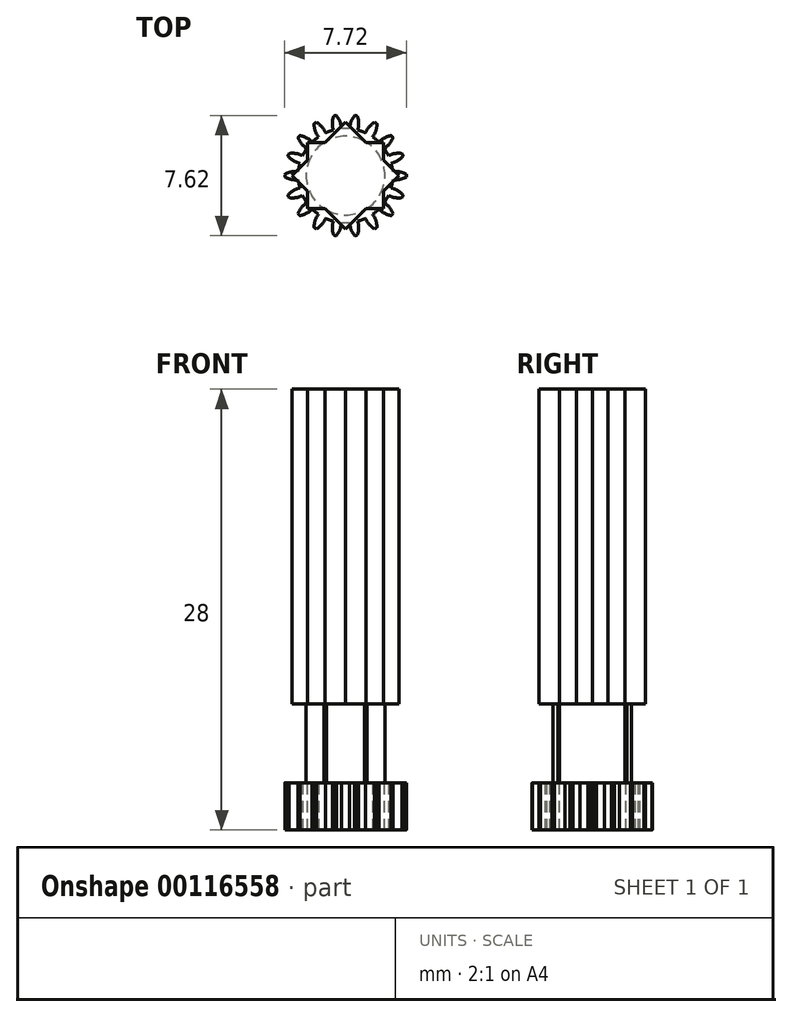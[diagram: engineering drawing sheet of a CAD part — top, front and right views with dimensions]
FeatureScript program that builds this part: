
annotation { "Feature Type Name" : "Feature", "Feature Type Description" : "" }
export const myFeature = defineFeature(function(context is Context, id is Id, definition is map)
    precondition{}
    {
        {
            var Q0;
            Q0=qCreatedBy(makeId("Top.planeOp"),FACE);
            var sketch = newSketch(context, id + "F0", { "sketchPlane" : qUnion([Q0])});
            skArc(sketch, "E0", {"start": v(2.95, 0.52) * mm, "mid": v(2.97, 0.4) * mm, "end": v(2.99, 0.26) * mm, "construction": true});
            skArc(sketch, "E1", {"start": v(2.95, 0.52) * mm, "mid": v(2.97, 0.4) * mm, "end": v(2.99, 0.26) * mm});
            skArc(sketch, "E2.MirrorCS", {"start": v(2.95, -0.52) * mm, "mid": v(2.97, -0.4) * mm, "end": v(2.99, -0.26) * mm});
            skPoint(sketch, "E3", {"position": v(3.86, 0) * mm});
            skArc(sketch, "E4", {"start": v(3.86, 0.09) * mm, "mid": v(3.44, 0.24) * mm, "end": v(2.99, 0.26) * mm});
            skArc(sketch, "E5", {"start": v(3.86, 0.09) * mm, "mid": v(3.86, 0.04) * mm, "end": v(3.86, 0) * mm});
            skLineSegment(sketch, "E6", {"start": v(0, 0) * mm, "end": v(4.16, 0) * mm, "construction": true});
            skArc(sketch, "E7.MirrorCS", {"start": v(3.86, -0.09) * mm, "mid": v(3.44, -0.24) * mm, "end": v(2.99, -0.26) * mm});
            skArc(sketch, "E8.MirrorCS", {"start": v(3.86, -0.09) * mm, "mid": v(3.86, -0.04) * mm, "end": v(3.86, 0) * mm});
            skLineSegment(sketch, "E9", {"start": v(0, 0) * mm, "end": v(2.95, 0.52) * mm});
            skLineSegment(sketch, "E10", {"start": v(0, 0) * mm, "end": v(2.95, -0.52) * mm});
            skSolve(sketch);
        }
        {
            var Q0;
            Q0=qSketchRegion(id+"F0",true);
            extrude(context, id + "F1", {"entities" : qUnion([Q0]), "depth" : 3 * mm});
        }
        {
            var Q0;
            Q0=makeQuery(id+"F1.opExtrude","SWEPT_BODY",BODY,{"disambiguationData":[OSD([sQuery(id+"F0.wireOp",EDGE,"E1"),sQuery(id+"F0.wireOp",EDGE,"E2.MirrorCS"),sQuery(id+"F0.wireOp",EDGE,"E4"),sQuery(id+"F0.wireOp",EDGE,"E5"),sQuery(id+"F0.wireOp",EDGE,"E7.MirrorCS"),sQuery(id+"F0.wireOp",EDGE,"E8.MirrorCS"),sQuery(id+"F0.wireOp",EDGE,"E9"),sQuery(id+"F0.wireOp",EDGE,"E10")])]});
            var Q1;
            Q1=makeQuery(id+"F1.opExtrude","SWEPT_EDGE",EDGE,{"disambiguationData":[OSD([sQuery(id+"F0.wireOp",EDGE,"E9"),sQuery(id+"F0.wireOp",EDGE,"E10")])]});
            circularPattern(context, id + "F2", {"operationType" : NewBodyOperationType.ADD, "entities" : qUnion([Q0]), "axis" : qUnion([Q1]), "angle" : 20 * degree, "instanceCount" : 18});
        }
        {
            var Q0;
            Q0=qSketchRegion(id+"F0",true);
            extrude(context, id + "F3", {"entities" : qUnion([Q0]), "depth" : 3 * mm});
        }
        {
            var Q0;
            Q0=makeQuery(id+"F1.opExtrude","CAP_FACE",FACE,{"disambiguationData":[OSD([sQuery(id+"F0.wireOp",EDGE,"Pb6nrEPp-SJh7-syUI-6Dz9-aLrEaNv6bWqD"),sQuery(id+"F0.wireOp",EDGE,"E1"),sQuery(id+"F0.wireOp",EDGE,"xMCTbKjx-bBFs-oRzr-sJjZ-jvfvOUALp0gi"),sQuery(id+"F0.wireOp",EDGE,"LEszv8Jj-5ZlA-iPn8-BHO1-omDbxf6y6Z2k"),sQuery(id+"F0.wireOp",EDGE,"88d082c0-6565-44ed-966f-5d657ca2ec560.MirrorCS"),sQuery(id+"F0.wireOp",EDGE,"E2.MirrorCS"),sQuery(id+"F0.wireOp",EDGE,"91265b68-e2b7-404f-b8fe-75b5f12c093b0.MirrorCS"),sQuery(id+"F0.wireOp",EDGE,"1d9e2677-8dce-4da0-891b-71f10a0ff0ad0.MirrorCS"),sQuery(id+"F0.wireOp",EDGE,"29e68c91-4fe4-4bf7-b556-72e67ca85e0b.1.0"),sQuery(id+"F0.wireOp",EDGE,"29e68c91-4fe4-4bf7-b556-72e67ca85e0b.1.1"),sQuery(id+"F0.wireOp",EDGE,"29e68c91-4fe4-4bf7-b556-72e67ca85e0b.1.2"),sQuery(id+"F0.wireOp",EDGE,"29e68c91-4fe4-4bf7-b556-72e67ca85e0b.1.3"),sQuery(id+"F0.wireOp",EDGE,"29e68c91-4fe4-4bf7-b556-72e67ca85e0b.1.4"),sQuery(id+"F0.wireOp",EDGE,"29e68c91-4fe4-4bf7-b556-72e67ca85e0b.1.5"),sQuery(id+"F0.wireOp",EDGE,"29e68c91-4fe4-4bf7-b556-72e67ca85e0b.1.7"),sQuery(id+"F0.wireOp",EDGE,"29e68c91-4fe4-4bf7-b556-72e67ca85e0b.1.8"),sQuery(id+"F0.wireOp",EDGE,"29e68c91-4fe4-4bf7-b556-72e67ca85e0b.2.0"),sQuery(id+"F0.wireOp",EDGE,"29e68c91-4fe4-4bf7-b556-72e67ca85e0b.2.1"),sQuery(id+"F0.wireOp",EDGE,"29e68c91-4fe4-4bf7-b556-72e67ca85e0b.2.2"),sQuery(id+"F0.wireOp",EDGE,"29e68c91-4fe4-4bf7-b556-72e67ca85e0b.2.3"),sQuery(id+"F0.wireOp",EDGE,"29e68c91-4fe4-4bf7-b556-72e67ca85e0b.2.4"),sQuery(id+"F0.wireOp",EDGE,"29e68c91-4fe4-4bf7-b556-72e67ca85e0b.2.5"),sQuery(id+"F0.wireOp",EDGE,"29e68c91-4fe4-4bf7-b556-72e67ca85e0b.2.7"),sQuery(id+"F0.wireOp",EDGE,"29e68c91-4fe4-4bf7-b556-72e67ca85e0b.2.8"),sQuery(id+"F0.wireOp",EDGE,"29e68c91-4fe4-4bf7-b556-72e67ca85e0b.3.0"),sQuery(id+"F0.wireOp",EDGE,"29e68c91-4fe4-4bf7-b556-72e67ca85e0b.3.1"),sQuery(id+"F0.wireOp",EDGE,"29e68c91-4fe4-4bf7-b556-72e67ca85e0b.3.2"),sQuery(id+"F0.wireOp",EDGE,"29e68c91-4fe4-4bf7-b556-72e67ca85e0b.3.3"),sQuery(id+"F0.wireOp",EDGE,"29e68c91-4fe4-4bf7-b556-72e67ca85e0b.3.4"),sQuery(id+"F0.wireOp",EDGE,"29e68c91-4fe4-4bf7-b556-72e67ca85e0b.3.5"),sQuery(id+"F0.wireOp",EDGE,"29e68c91-4fe4-4bf7-b556-72e67ca85e0b.3.7"),sQuery(id+"F0.wireOp",EDGE,"29e68c91-4fe4-4bf7-b556-72e67ca85e0b.3.8"),sQuery(id+"F0.wireOp",EDGE,"29e68c91-4fe4-4bf7-b556-72e67ca85e0b.4.0"),sQuery(id+"F0.wireOp",EDGE,"29e68c91-4fe4-4bf7-b556-72e67ca85e0b.4.1"),sQuery(id+"F0.wireOp",EDGE,"29e68c91-4fe4-4bf7-b556-72e67ca85e0b.4.2"),sQuery(id+"F0.wireOp",EDGE,"29e68c91-4fe4-4bf7-b556-72e67ca85e0b.4.3"),sQuery(id+"F0.wireOp",EDGE,"29e68c91-4fe4-4bf7-b556-72e67ca85e0b.4.4"),sQuery(id+"F0.wireOp",EDGE,"29e68c91-4fe4-4bf7-b556-72e67ca85e0b.4.5"),sQuery(id+"F0.wireOp",EDGE,"29e68c91-4fe4-4bf7-b556-72e67ca85e0b.4.7"),sQuery(id+"F0.wireOp",EDGE,"29e68c91-4fe4-4bf7-b556-72e67ca85e0b.4.8"),sQuery(id+"F0.wireOp",EDGE,"29e68c91-4fe4-4bf7-b556-72e67ca85e0b.5.0"),sQuery(id+"F0.wireOp",EDGE,"29e68c91-4fe4-4bf7-b556-72e67ca85e0b.5.1"),sQuery(id+"F0.wireOp",EDGE,"29e68c91-4fe4-4bf7-b556-72e67ca85e0b.5.2"),sQuery(id+"F0.wireOp",EDGE,"29e68c91-4fe4-4bf7-b556-72e67ca85e0b.5.3"),sQuery(id+"F0.wireOp",EDGE,"29e68c91-4fe4-4bf7-b556-72e67ca85e0b.5.4"),sQuery(id+"F0.wireOp",EDGE,"29e68c91-4fe4-4bf7-b556-72e67ca85e0b.5.5"),sQuery(id+"F0.wireOp",EDGE,"29e68c91-4fe4-4bf7-b556-72e67ca85e0b.5.7"),sQuery(id+"F0.wireOp",EDGE,"29e68c91-4fe4-4bf7-b556-72e67ca85e0b.5.8"),sQuery(id+"F0.wireOp",EDGE,"29e68c91-4fe4-4bf7-b556-72e67ca85e0b.6.0"),sQuery(id+"F0.wireOp",EDGE,"29e68c91-4fe4-4bf7-b556-72e67ca85e0b.6.1"),sQuery(id+"F0.wireOp",EDGE,"29e68c91-4fe4-4bf7-b556-72e67ca85e0b.6.2"),sQuery(id+"F0.wireOp",EDGE,"29e68c91-4fe4-4bf7-b556-72e67ca85e0b.6.3"),sQuery(id+"F0.wireOp",EDGE,"29e68c91-4fe4-4bf7-b556-72e67ca85e0b.6.4"),sQuery(id+"F0.wireOp",EDGE,"29e68c91-4fe4-4bf7-b556-72e67ca85e0b.6.5"),sQuery(id+"F0.wireOp",EDGE,"29e68c91-4fe4-4bf7-b556-72e67ca85e0b.6.7"),sQuery(id+"F0.wireOp",EDGE,"29e68c91-4fe4-4bf7-b556-72e67ca85e0b.6.8"),sQuery(id+"F0.wireOp",EDGE,"29e68c91-4fe4-4bf7-b556-72e67ca85e0b.7.0"),sQuery(id+"F0.wireOp",EDGE,"29e68c91-4fe4-4bf7-b556-72e67ca85e0b.7.1"),sQuery(id+"F0.wireOp",EDGE,"29e68c91-4fe4-4bf7-b556-72e67ca85e0b.7.2"),sQuery(id+"F0.wireOp",EDGE,"29e68c91-4fe4-4bf7-b556-72e67ca85e0b.7.3"),sQuery(id+"F0.wireOp",EDGE,"29e68c91-4fe4-4bf7-b556-72e67ca85e0b.7.4"),sQuery(id+"F0.wireOp",EDGE,"29e68c91-4fe4-4bf7-b556-72e67ca85e0b.7.5"),sQuery(id+"F0.wireOp",EDGE,"29e68c91-4fe4-4bf7-b556-72e67ca85e0b.7.7"),sQuery(id+"F0.wireOp",EDGE,"29e68c91-4fe4-4bf7-b556-72e67ca85e0b.7.8"),sQuery(id+"F0.wireOp",EDGE,"29e68c91-4fe4-4bf7-b556-72e67ca85e0b.8.0"),sQuery(id+"F0.wireOp",EDGE,"29e68c91-4fe4-4bf7-b556-72e67ca85e0b.8.1"),sQuery(id+"F0.wireOp",EDGE,"29e68c91-4fe4-4bf7-b556-72e67ca85e0b.8.2"),sQuery(id+"F0.wireOp",EDGE,"29e68c91-4fe4-4bf7-b556-72e67ca85e0b.8.3"),sQuery(id+"F0.wireOp",EDGE,"29e68c91-4fe4-4bf7-b556-72e67ca85e0b.8.4"),sQuery(id+"F0.wireOp",EDGE,"29e68c91-4fe4-4bf7-b556-72e67ca85e0b.8.5"),sQuery(id+"F0.wireOp",EDGE,"29e68c91-4fe4-4bf7-b556-72e67ca85e0b.8.7"),sQuery(id+"F0.wireOp",EDGE,"29e68c91-4fe4-4bf7-b556-72e67ca85e0b.8.8"),sQuery(id+"F0.wireOp",EDGE,"29e68c91-4fe4-4bf7-b556-72e67ca85e0b.9.0"),sQuery(id+"F0.wireOp",EDGE,"29e68c91-4fe4-4bf7-b556-72e67ca85e0b.9.1"),sQuery(id+"F0.wireOp",EDGE,"29e68c91-4fe4-4bf7-b556-72e67ca85e0b.9.2"),sQuery(id+"F0.wireOp",EDGE,"29e68c91-4fe4-4bf7-b556-72e67ca85e0b.9.3"),sQuery(id+"F0.wireOp",EDGE,"29e68c91-4fe4-4bf7-b556-72e67ca85e0b.9.4"),sQuery(id+"F0.wireOp",EDGE,"29e68c91-4fe4-4bf7-b556-72e67ca85e0b.9.5"),sQuery(id+"F0.wireOp",EDGE,"29e68c91-4fe4-4bf7-b556-72e67ca85e0b.9.7"),sQuery(id+"F0.wireOp",EDGE,"29e68c91-4fe4-4bf7-b556-72e67ca85e0b.9.8"),sQuery(id+"F0.wireOp",EDGE,"29e68c91-4fe4-4bf7-b556-72e67ca85e0b.10.0"),sQuery(id+"F0.wireOp",EDGE,"29e68c91-4fe4-4bf7-b556-72e67ca85e0b.10.1"),sQuery(id+"F0.wireOp",EDGE,"29e68c91-4fe4-4bf7-b556-72e67ca85e0b.10.2"),sQuery(id+"F0.wireOp",EDGE,"29e68c91-4fe4-4bf7-b556-72e67ca85e0b.10.3"),sQuery(id+"F0.wireOp",EDGE,"29e68c91-4fe4-4bf7-b556-72e67ca85e0b.10.4"),sQuery(id+"F0.wireOp",EDGE,"29e68c91-4fe4-4bf7-b556-72e67ca85e0b.10.5"),sQuery(id+"F0.wireOp",EDGE,"29e68c91-4fe4-4bf7-b556-72e67ca85e0b.10.7"),sQuery(id+"F0.wireOp",EDGE,"29e68c91-4fe4-4bf7-b556-72e67ca85e0b.10.8"),sQuery(id+"F0.wireOp",EDGE,"29e68c91-4fe4-4bf7-b556-72e67ca85e0b.11.0"),sQuery(id+"F0.wireOp",EDGE,"29e68c91-4fe4-4bf7-b556-72e67ca85e0b.11.1"),sQuery(id+"F0.wireOp",EDGE,"29e68c91-4fe4-4bf7-b556-72e67ca85e0b.11.2"),sQuery(id+"F0.wireOp",EDGE,"29e68c91-4fe4-4bf7-b556-72e67ca85e0b.11.3"),sQuery(id+"F0.wireOp",EDGE,"29e68c91-4fe4-4bf7-b556-72e67ca85e0b.11.4"),sQuery(id+"F0.wireOp",EDGE,"29e68c91-4fe4-4bf7-b556-72e67ca85e0b.11.5"),sQuery(id+"F0.wireOp",EDGE,"29e68c91-4fe4-4bf7-b556-72e67ca85e0b.11.7"),sQuery(id+"F0.wireOp",EDGE,"29e68c91-4fe4-4bf7-b556-72e67ca85e0b.11.8"),sQuery(id+"F0.wireOp",EDGE,"29e68c91-4fe4-4bf7-b556-72e67ca85e0b.12.0"),sQuery(id+"F0.wireOp",EDGE,"29e68c91-4fe4-4bf7-b556-72e67ca85e0b.12.1"),sQuery(id+"F0.wireOp",EDGE,"29e68c91-4fe4-4bf7-b556-72e67ca85e0b.12.2"),sQuery(id+"F0.wireOp",EDGE,"29e68c91-4fe4-4bf7-b556-72e67ca85e0b.12.3"),sQuery(id+"F0.wireOp",EDGE,"29e68c91-4fe4-4bf7-b556-72e67ca85e0b.12.4"),sQuery(id+"F0.wireOp",EDGE,"29e68c91-4fe4-4bf7-b556-72e67ca85e0b.12.5"),sQuery(id+"F0.wireOp",EDGE,"29e68c91-4fe4-4bf7-b556-72e67ca85e0b.12.7"),sQuery(id+"F0.wireOp",EDGE,"29e68c91-4fe4-4bf7-b556-72e67ca85e0b.12.8"),sQuery(id+"F0.wireOp",EDGE,"29e68c91-4fe4-4bf7-b556-72e67ca85e0b.13.0"),sQuery(id+"F0.wireOp",EDGE,"29e68c91-4fe4-4bf7-b556-72e67ca85e0b.13.1"),sQuery(id+"F0.wireOp",EDGE,"29e68c91-4fe4-4bf7-b556-72e67ca85e0b.13.2"),sQuery(id+"F0.wireOp",EDGE,"29e68c91-4fe4-4bf7-b556-72e67ca85e0b.13.3"),sQuery(id+"F0.wireOp",EDGE,"29e68c91-4fe4-4bf7-b556-72e67ca85e0b.13.4"),sQuery(id+"F0.wireOp",EDGE,"29e68c91-4fe4-4bf7-b556-72e67ca85e0b.13.5"),sQuery(id+"F0.wireOp",EDGE,"29e68c91-4fe4-4bf7-b556-72e67ca85e0b.13.7"),sQuery(id+"F0.wireOp",EDGE,"29e68c91-4fe4-4bf7-b556-72e67ca85e0b.13.8"),sQuery(id+"F0.wireOp",EDGE,"29e68c91-4fe4-4bf7-b556-72e67ca85e0b.14.0"),sQuery(id+"F0.wireOp",EDGE,"29e68c91-4fe4-4bf7-b556-72e67ca85e0b.14.1"),sQuery(id+"F0.wireOp",EDGE,"29e68c91-4fe4-4bf7-b556-72e67ca85e0b.14.2"),sQuery(id+"F0.wireOp",EDGE,"29e68c91-4fe4-4bf7-b556-72e67ca85e0b.14.3"),sQuery(id+"F0.wireOp",EDGE,"29e68c91-4fe4-4bf7-b556-72e67ca85e0b.14.4"),sQuery(id+"F0.wireOp",EDGE,"29e68c91-4fe4-4bf7-b556-72e67ca85e0b.14.5"),sQuery(id+"F0.wireOp",EDGE,"29e68c91-4fe4-4bf7-b556-72e67ca85e0b.14.7"),sQuery(id+"F0.wireOp",EDGE,"29e68c91-4fe4-4bf7-b556-72e67ca85e0b.14.8"),sQuery(id+"F0.wireOp",EDGE,"29e68c91-4fe4-4bf7-b556-72e67ca85e0b.15.0"),sQuery(id+"F0.wireOp",EDGE,"29e68c91-4fe4-4bf7-b556-72e67ca85e0b.15.1"),sQuery(id+"F0.wireOp",EDGE,"29e68c91-4fe4-4bf7-b556-72e67ca85e0b.15.2"),sQuery(id+"F0.wireOp",EDGE,"29e68c91-4fe4-4bf7-b556-72e67ca85e0b.15.3"),sQuery(id+"F0.wireOp",EDGE,"29e68c91-4fe4-4bf7-b556-72e67ca85e0b.15.4"),sQuery(id+"F0.wireOp",EDGE,"29e68c91-4fe4-4bf7-b556-72e67ca85e0b.15.5"),sQuery(id+"F0.wireOp",EDGE,"29e68c91-4fe4-4bf7-b556-72e67ca85e0b.15.7"),sQuery(id+"F0.wireOp",EDGE,"29e68c91-4fe4-4bf7-b556-72e67ca85e0b.15.8"),sQuery(id+"F0.wireOp",EDGE,"29e68c91-4fe4-4bf7-b556-72e67ca85e0b.16.0"),sQuery(id+"F0.wireOp",EDGE,"29e68c91-4fe4-4bf7-b556-72e67ca85e0b.16.1"),sQuery(id+"F0.wireOp",EDGE,"29e68c91-4fe4-4bf7-b556-72e67ca85e0b.16.2"),sQuery(id+"F0.wireOp",EDGE,"29e68c91-4fe4-4bf7-b556-72e67ca85e0b.16.3"),sQuery(id+"F0.wireOp",EDGE,"29e68c91-4fe4-4bf7-b556-72e67ca85e0b.16.4"),sQuery(id+"F0.wireOp",EDGE,"29e68c91-4fe4-4bf7-b556-72e67ca85e0b.16.5"),sQuery(id+"F0.wireOp",EDGE,"29e68c91-4fe4-4bf7-b556-72e67ca85e0b.16.7"),sQuery(id+"F0.wireOp",EDGE,"29e68c91-4fe4-4bf7-b556-72e67ca85e0b.16.8"),sQuery(id+"F0.wireOp",EDGE,"29e68c91-4fe4-4bf7-b556-72e67ca85e0b.17.0"),sQuery(id+"F0.wireOp",EDGE,"29e68c91-4fe4-4bf7-b556-72e67ca85e0b.17.1"),sQuery(id+"F0.wireOp",EDGE,"29e68c91-4fe4-4bf7-b556-72e67ca85e0b.17.2"),sQuery(id+"F0.wireOp",EDGE,"29e68c91-4fe4-4bf7-b556-72e67ca85e0b.17.3"),sQuery(id+"F0.wireOp",EDGE,"29e68c91-4fe4-4bf7-b556-72e67ca85e0b.17.4"),sQuery(id+"F0.wireOp",EDGE,"29e68c91-4fe4-4bf7-b556-72e67ca85e0b.17.5"),sQuery(id+"F0.wireOp",EDGE,"29e68c91-4fe4-4bf7-b556-72e67ca85e0b.17.7"),sQuery(id+"F0.wireOp",EDGE,"29e68c91-4fe4-4bf7-b556-72e67ca85e0b.17.8")])],"isStart":false});
            var sketch = newSketch(context, id + "F4", { "sketchPlane" : qUnion([Q0])});
            skLineSegment(sketch, "E11.bottom", {"start": v(2.4, -2.1) * mm, "end": v(-2.4, -2.1) * mm});
            skLineSegment(sketch, "E11.top", {"start": v(2.4, 2.1) * mm, "end": v(-2.4, 2.1) * mm});
            skLineSegment(sketch, "E11.left", {"start": v(2.4, -2.1) * mm, "end": v(2.4, 2.1) * mm});
            skLineSegment(sketch, "E11.right", {"start": v(-2.4, -2.1) * mm, "end": v(-2.4, 2.1) * mm});
            skPoint(sketch, "E11.middle", {"position": v(0, 0) * mm});
            skLineSegment(sketch, "E12", {"start": v(-3.4, 0) * mm, "end": v(0, 3.4) * mm});
            skLineSegment(sketch, "E13", {"start": v(0, 3.4) * mm, "end": v(3.4, 0) * mm});
            skLineSegment(sketch, "E14", {"start": v(3.4, 0) * mm, "end": v(0, -3.4) * mm});
            skLineSegment(sketch, "E15", {"start": v(0, -3.4) * mm, "end": v(-3.4, 0) * mm});
            skSolve(sketch);
        }
        {
            var Q0;
            Q0=qSketchRegion(id+"F4",true);
            extrude(context, id + "F5", {"entities" : qUnion([Q0]), "operationType" : NewBodyOperationType.ADD, "depth" : 25 * mm});
        }
        {
            var Q0;
            {var subQ0=sQuery(id+"F0.wireOp",EDGE,"E7.MirrorCS");var subQ2=sQuery(id+"F0.wireOp",EDGE,"E4");var subQ4=sQuery(id+"F0.wireOp",EDGE,"E8.MirrorCS");var subQ5=sQuery(id+"F0.wireOp",EDGE,"E5");var subQ12=sQuery(id+"F0.wireOp",EDGE,"E2.MirrorCS");var subQ13=makeQuery(id+"F1.opExtrude","SWEPT_FACE",FACE,{"disambiguationData":[OSD([subQ12])]});var subQ14=sQuery(id+"F0.wireOp",EDGE,"E1");var subQ23=makeQuery(id+"F1.opExtrude","CAP_FACE",FACE,{"disambiguationData":[OSD([subQ14,subQ12,subQ2,subQ5,subQ0,subQ4,sQuery(id+"F0.wireOp",EDGE,"E9"),sQuery(id+"F0.wireOp",EDGE,"E10")])],"isStart":false});Q0=makeQuery(id+"F5.boolean.opBoolean","SPLIT",FACE,{"disambiguationData":[TD([subQ13])],"derivedFrom":makeQuery(id+"F2.boolean.opBoolean","MERGE",FACE,{"derivedFrom":[subQ23,makeQuery(id+"F2.opPattern","COPY",FACE,{"derivedFrom":subQ23,"instanceName":"1"}),makeQuery(id+"F2.opPattern","COPY",FACE,{"derivedFrom":subQ23,"instanceName":"2"}),makeQuery(id+"F2.opPattern","COPY",FACE,{"derivedFrom":subQ23,"instanceName":"3"}),makeQuery(id+"F2.opPattern","COPY",FACE,{"derivedFrom":subQ23,"instanceName":"4"}),makeQuery(id+"F2.opPattern","COPY",FACE,{"derivedFrom":subQ23,"instanceName":"5"}),makeQuery(id+"F2.opPattern","COPY",FACE,{"derivedFrom":subQ23,"instanceName":"6"}),makeQuery(id+"F2.opPattern","COPY",FACE,{"derivedFrom":subQ23,"instanceName":"7"}),makeQuery(id+"F2.opPattern","COPY",FACE,{"derivedFrom":subQ23,"instanceName":"8"}),makeQuery(id+"F2.opPattern","COPY",FACE,{"derivedFrom":subQ23,"instanceName":"9"}),makeQuery(id+"F2.opPattern","COPY",FACE,{"derivedFrom":subQ23,"instanceName":"10"}),makeQuery(id+"F2.opPattern","COPY",FACE,{"derivedFrom":subQ23,"instanceName":"11"}),makeQuery(id+"F2.opPattern","COPY",FACE,{"derivedFrom":subQ23,"instanceName":"12"}),makeQuery(id+"F2.opPattern","COPY",FACE,{"derivedFrom":subQ23,"instanceName":"13"}),makeQuery(id+"F2.opPattern","COPY",FACE,{"derivedFrom":subQ23,"instanceName":"14"}),makeQuery(id+"F2.opPattern","COPY",FACE,{"derivedFrom":subQ23,"instanceName":"15"}),makeQuery(id+"F2.opPattern","COPY",FACE,{"derivedFrom":subQ23,"instanceName":"16"}),makeQuery(id+"F2.opPattern","COPY",FACE,{"derivedFrom":subQ23,"instanceName":"17"})]})});}
            var sketch = newSketch(context, id + "F6", { "sketchPlane" : qUnion([Q0])});
            skCircle(sketch, "E16", {"center": v(0, 0) * mm, "radius": 2.5 * mm});
            skCircle(sketch, "E17", {"center": v(0, 0) * mm, "radius": 5 * mm});
            skSolve(sketch);
        }
        {
            var Q0;
            Q0 = qSketchRegion(id + "F6", true);
            extrude(context, id + "F7", {"entities" : qUnion([Q0]), "operationType" : NewBodyOperationType.REMOVE, "depth" : 5 * mm});
        }
    });
